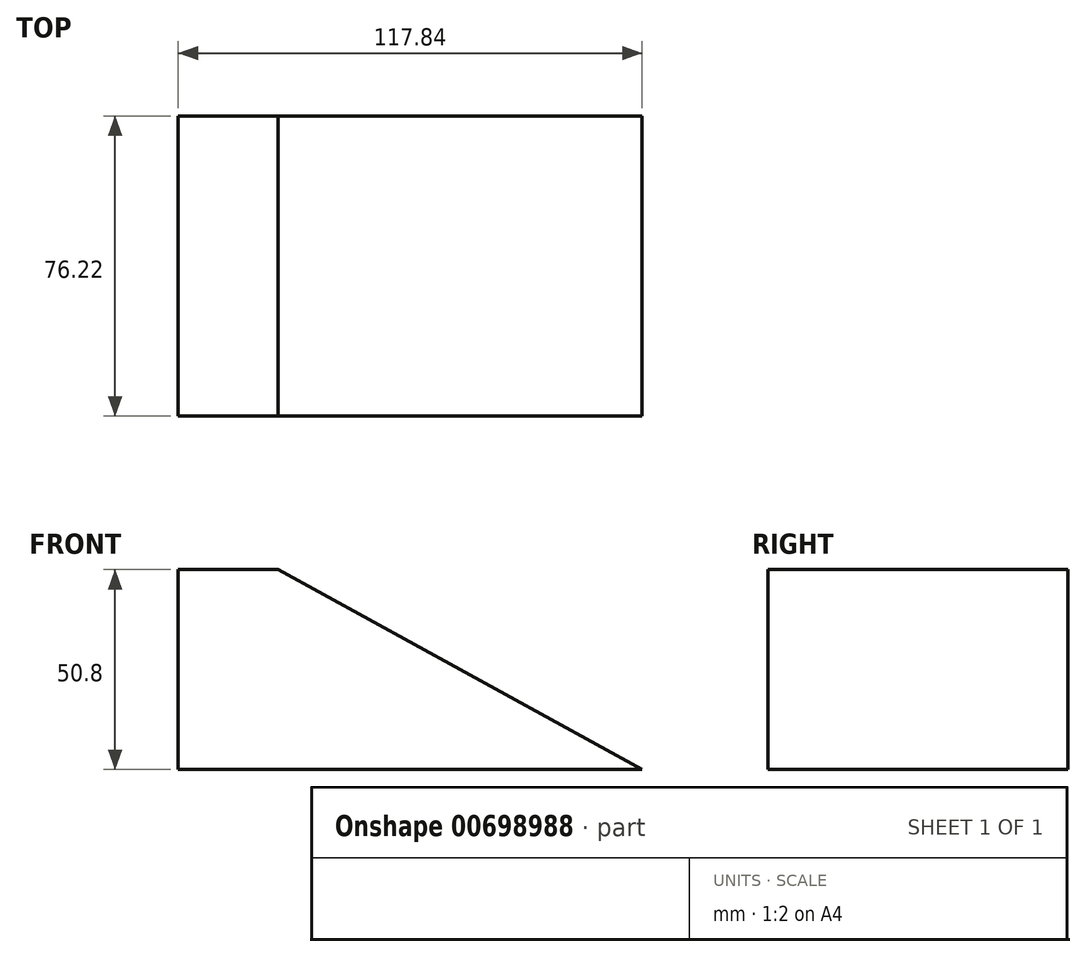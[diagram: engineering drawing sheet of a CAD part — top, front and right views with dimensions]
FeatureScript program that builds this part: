
annotation { "Feature Type Name" : "Feature", "Feature Type Description" : "" }
export const myFeature = defineFeature(function(context is Context, id is Id, definition is map)
    precondition{}
    {
        {
            var Q0;
            Q0=qCreatedBy(makeId("Top.planeOp"),FACE);
            var sketch = newSketch(context, id + "F0", { "sketchPlane" : qUnion([Q0])});
            skLineSegment(sketch, "E0.bottom", {"start": v(46.22, -38.1) * mm, "end": v(-46.22, -38.1) * mm});
            skLineSegment(sketch, "E0.top", {"start": v(46.22, 38.1) * mm, "end": v(-46.22, 38.1) * mm});
            skLineSegment(sketch, "E0.left", {"start": v(46.22, -38.1) * mm, "end": v(46.22, 38.1) * mm});
            skLineSegment(sketch, "E0.right", {"start": v(-46.22, -38.1) * mm, "end": v(-46.22, 38.1) * mm});
            skPoint(sketch, "E0.middle", {"position": v(0, 0) * mm});
            skSolve(sketch);
        }
        {
            var Q0;
            Q0 = qSketchRegion(id + "F0", true);
            extrude(context, id + "F1", {"entities" : qUnion([Q0]), "depth" : 50.8 * mm, "offsetDistance" : 25.4 * mm});
        }
        {
            var Q0;
            Q0=makeQuery(id+"F1.opExtrude","SWEPT_FACE",FACE,{"disambiguationData":[OSD([sQuery(id+"F0.wireOp",EDGE,"E0.bottom")])]});
            var sketch = newSketch(context, id + "F2", { "sketchPlane" : qUnion([Q0])});
            skLineSegment(sketch, "E1", {"start": v(-46.22, 50.8) * mm, "end": v(46.22, 0) * mm});
            skSolve(sketch);
        }
        {
            var Q0;
            Q0=makeQuery(id+"F2.imprint","IMPRINT",FACE,{"disambiguationData":[TD([[makeQuery(id+"F2.imprint","IMPRINT",EDGE,{"derivedFrom":sQuery(id+"F2.wireOp",EDGE,"E1")}),1.0]])]});
            extrude(context, id + "F3", {"entities" : qUnion([Q0]), "operationType" : NewBodyOperationType.REMOVE, "oppositeDirection" : true, "depth" : 127 * mm, "offsetDistance" : 25.4 * mm});
        }
        {
            var Q0;
            Q0=makeQuery(id+"F1.opExtrude","SWEPT_FACE",FACE,{"disambiguationData":[OSD([sQuery(id+"F0.wireOp",EDGE,"E0.right")])]});
            extrude(context, id + "F4", {"entities" : qUnion([Q0]), "operationType" : NewBodyOperationType.ADD, "depth" : 25.4 * mm, "offsetDistance" : 25.4 * mm});
        }
    });
